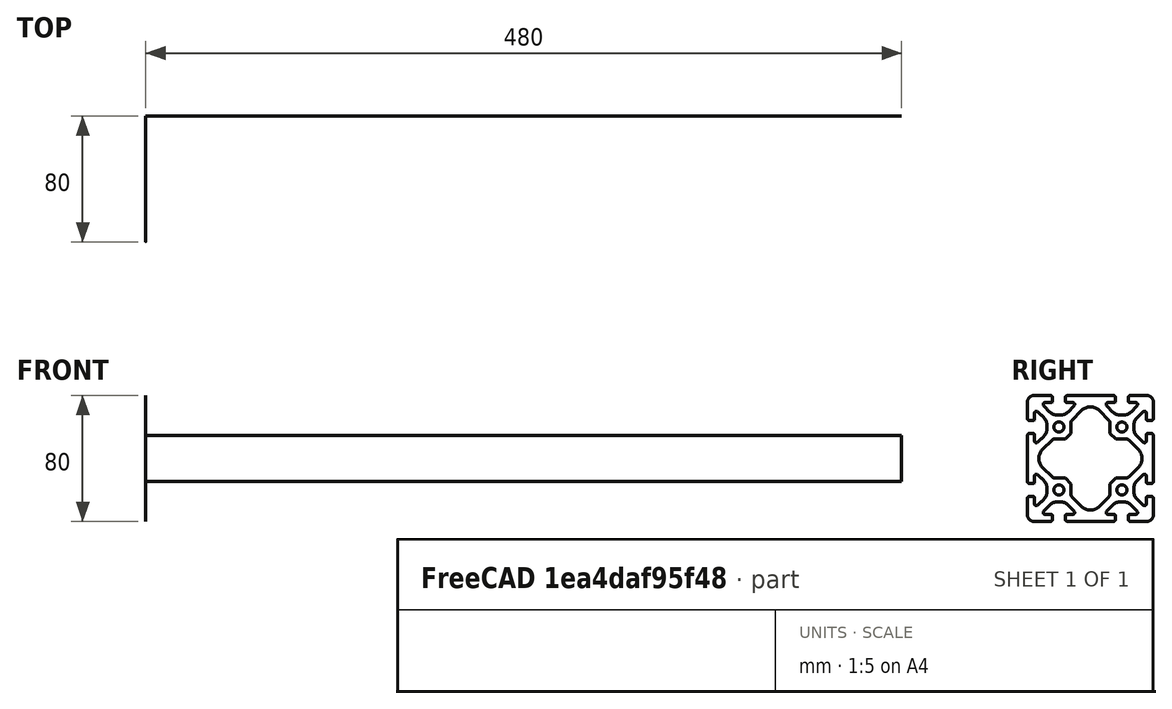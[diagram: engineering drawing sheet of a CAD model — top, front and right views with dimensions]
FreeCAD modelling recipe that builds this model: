
FCSTD DOCUMENT  (FreeCAD 0.21R38887 (Git))
Label: станок_сборка
License: All rights reserved
LicenseURL: http://en.wikipedia.org/wiki/All_rights_reserved
objects: App::FeaturePython×14, Part::FeaturePython×11, App::Link×2
note: 10 computed .brp shape members not serialized (recipe doc carries the construction recipe); baked Part::Feature solids carry a one-line shape summary decoded from their .brp
EXTERNAL_REF file=Станина/СтанинаСборка.FCStd obj=Assembly003
EXTERNAL_REF file=Стол/СборкаСтола.FCStd obj=Assembly

FEATURE [App::Link] Link  label="СборкаСтанины"
  AutoLinkLabel = false
  AutoPlacement = true
  LinkedObject = -> <external Станина/СтанинаСборка.FCStd>#Assembly003
  SyncGroupVisibility = false
  TreeRank = 0
  _LinkOwner = 31
  _LinkVersion = 1
FEATURE [App::Link] Link001  label="СборкаСтола"
  AutoLinkLabel = false
  AutoPlacement = true
  LinkPlacement = pos=(362.85,437.507,143.56) rot=(0.707107,0,0.707107;3.14159rad)
  LinkedObject = -> <external Стол/СборкаСтола.FCStd>#Assembly
  Placement = pos=(362.85,437.507,143.56) rot=(0.707107,0,0.707107;3.14159rad)
  SyncGroupVisibility = false
  TreeRank = 0
  _LinkOwner = 31
  _LinkVersion = 1
FEATURE [Part::FeaturePython] Parts  # WARN: FeaturePython — macro-defined, semantics opaque (R4)
  Group = -> [Link,Link001]
  GroupMode = 0
  InvalidShape = false
  TreeRank = 0
  ValidateShape = false
  _LinkVersion = 1
FEATURE [Part::FeaturePython] Assembly  # WARN: FeaturePython — macro-defined, semantics opaque (R4)
  AutoRelax = true
  BuildShape = 0
  Freeze = false
  Group = -> [Constraints,Elements,Parts]
  InvalidShape = false
  TreeRank = 0
  ValidateShape = false
  Verbose = false
  _LinkVersion = 1
  _SolverType = 1
  _Version = 1
FEATURE [App::FeaturePython] Constraints  # WARN: FeaturePython — macro-defined, semantics opaque (R4)
  Group = -> [Constraint001,Constraint,Constraint002]
  TreeRank = 0
  _LinkVersion = 1
  _Version = 1
FEATURE [App::FeaturePython] Elements  # WARN: FeaturePython — macro-defined, semantics opaque (R4)
  Group = -> [Element,Element001,_Element,_Element001,Element002,_Element002,_Element003,_Element004,_Element005]
  TreeRank = 0
  _LinkVersion = 1
FEATURE [Part::FeaturePython] Element  # link proxy (typed FeaturePython)
  Detach = false
  InvalidShape = false
  LinkTransform = true
  LinkedObject = -> Link [1.$Element152.]
  TreeRank = 0
  ValidateShape = false
  _LinkVersion = 1
  _Parent = -> Elements
FEATURE [Part::FeaturePython] Element001  # link proxy (typed FeaturePython)
  Detach = false
  InvalidShape = false
  LinkTransform = true
  LinkedObject = -> Link001 [1.$Element029.]
  TreeRank = 0
  ValidateShape = false
  _LinkVersion = 1
  _Parent = -> Elements
FEATURE [App::FeaturePython] Constraint  label="AxialAlignment"  # WARN: FeaturePython — macro-defined, semantics opaque (R4)
  Angle = 0
  AnglePitch = 0
  AngleRoll = 0
  Disabled = false
  Group = -> [ElementLink,ElementLink001,ElementLink005,ElementLink006,ElementLink009,ElementLink010]
  LockAngle = false
  Multiply = false
  TreeRank = 0
  _ConstraintType = 36
  _LinkVersion = 1
  _Parent = -> Constraints
FEATURE [App::FeaturePython] ElementLink  label="Element001"  # link proxy (typed FeaturePython)
  LinkTransform = true
  LinkedObject = -> Element001
  TreeRank = 0
  _LinkVersion = 1
  _Parent = -> Constraint
FEATURE [App::FeaturePython] ElementLink001  label="Element"  # link proxy (typed FeaturePython)
  LinkTransform = true
  LinkedObject = -> Element
  TreeRank = 0
  _LinkVersion = 1
  _Parent = -> Constraint
FEATURE [App::FeaturePython] Constraint001  label="Locked"  # WARN: FeaturePython — macro-defined, semantics opaque (R4)
  Disabled = false
  Group = -> [ElementLink002]
  TreeRank = 0
  _ConstraintType = 0
  _LinkVersion = 1
  _Parent = -> Constraints
FEATURE [App::FeaturePython] ElementLink002  label="_Element"  # link proxy (typed FeaturePython)
  LinkTransform = true
  LinkedObject = -> _Element
  TreeRank = 0
  _LinkVersion = 1
  _Parent = -> Constraint001
FEATURE [Part::FeaturePython] _Element  # link proxy (typed FeaturePython)
  Detach = false
  InvalidShape = false
  LinkTransform = true
  LinkedObject = -> Link [1.$Element154.]
  TreeRank = 0
  ValidateShape = false
  _LinkVersion = 1
  _Parent = -> Elements
FEATURE [App::FeaturePython] Constraint002  label="LineHorizontal"  # WARN: FeaturePython — macro-defined, semantics opaque (R4)
  Disabled = false
  Group = -> [ElementLink003,ElementLink004]
  TreeRank = 0
  _ConstraintType = 23
  _LinkVersion = 1
  _Parent = -> Constraints
FEATURE [App::FeaturePython] ElementLink003  label="_Element001"  # link proxy (typed FeaturePython)
  LinkTransform = true
  LinkedObject = -> _Element001
  TreeRank = 0
  _LinkVersion = 1
  _Parent = -> Constraint002
FEATURE [Part::FeaturePython] _Element001  # link proxy (typed FeaturePython)
  Detach = false
  InvalidShape = false
  LinkTransform = true
  LinkedObject = -> Link001 [1.$Element030.]
  TreeRank = 0
  ValidateShape = false
  _LinkVersion = 1
  _Parent = -> Elements
FEATURE [Part::FeaturePython] Element002  # link proxy (typed FeaturePython)
  Detach = false
  InvalidShape = false
  LinkTransform = true
  LinkedObject = -> Link [1.$_Element020.]
  TreeRank = 0
  ValidateShape = false
  _LinkVersion = 1
  _Parent = -> Elements
FEATURE [App::FeaturePython] ElementLink004  label="Element002"  # link proxy (typed FeaturePython)
  LinkTransform = true
  LinkedObject = -> Element002
  TreeRank = 0
  _LinkVersion = 1
  _Parent = -> Constraint002
FEATURE [App::FeaturePython] ElementLink005  label="_Element002"  # link proxy (typed FeaturePython)
  LinkTransform = true
  LinkedObject = -> _Element002
  TreeRank = 0
  _LinkVersion = 1
  _Parent = -> Constraint
FEATURE [Part::FeaturePython] _Element002  # link proxy (typed FeaturePython)
  Detach = false
  InvalidShape = false
  LinkTransform = true
  LinkedObject = -> Link001 [1.$Element031.]
  TreeRank = 0
  ValidateShape = false
  _LinkVersion = 1
  _Parent = -> Elements
FEATURE [App::FeaturePython] ElementLink006  label="_Element003"  # link proxy (typed FeaturePython)
  LinkTransform = true
  LinkedObject = -> _Element003
  TreeRank = 0
  _LinkVersion = 1
  _Parent = -> Constraint
FEATURE [Part::FeaturePython] _Element003  # link proxy (typed FeaturePython)
  Detach = false
  InvalidShape = false
  LinkTransform = true
  LinkedObject = -> Link [1.$Element156.]
  TreeRank = 0
  ValidateShape = false
  _LinkVersion = 1
  _Parent = -> Elements
FEATURE [App::FeaturePython] ElementLink009  label="_Element004"  # link proxy (typed FeaturePython)
  LinkTransform = true
  LinkedObject = -> _Element004
  TreeRank = 0
  _LinkVersion = 1
  _Parent = -> Constraint
FEATURE [Part::FeaturePython] _Element004  # link proxy (typed FeaturePython)
  Detach = false
  InvalidShape = false
  LinkTransform = true
  LinkedObject = -> Link001 [1.$Element032.]
  TreeRank = 0
  ValidateShape = false
  _LinkVersion = 1
  _Parent = -> Elements
FEATURE [App::FeaturePython] ElementLink010  label="_Element005"  # link proxy (typed FeaturePython)
  LinkTransform = true
  LinkedObject = -> _Element005
  TreeRank = 0
  _LinkVersion = 1
  _Parent = -> Constraint
FEATURE [Part::FeaturePython] _Element005  # link proxy (typed FeaturePython)
  Detach = false
  InvalidShape = false
  LinkTransform = true
  LinkedObject = -> Link [1.$Element158.]
  TreeRank = 0
  ValidateShape = false
  _LinkVersion = 1
  _Parent = -> Elements

RESOLVED EXTERNAL PARTS (link-assembly join: the EXTERNAL_REF files above that resolve inside this repo's crawl, each included once):
---- part Станина/СтанинаСборка.FCStd = doc fcstd_94fc6bfe06bf (92996 chars; too large to inline — full recipe in that document) ----
---- part Стол/СборкаСтола.FCStd = doc fcstd_60361f81c97c ----
FCSTD DOCUMENT  (FreeCAD 0.21R38887 (Git))
Label: СборкаСтола
License: All rights reserved
LicenseURL: http://en.wikipedia.org/wiki/All_rights_reserved
objects: App::FeaturePython×55, Part::FeaturePython×49, App::Link×4, App::LinkElement×4
note: 48 computed .brp shape members not serialized (recipe doc carries the construction recipe); baked Part::Feature solids carry a one-line shape summary decoded from their .brp
EXTERNAL_REF file=КронштейнГайки.FCStd obj=Body
EXTERNAL_REF file=Стол.FCStd obj=Body
EXTERNAL_REF file=HGH15CA.FCStd obj=Assembly
EXTERNAL_REF file=SFU1605.FCStd obj=Assembly

FEATURE [App::Link] Link  label="КронштейнГайкиX"
  AutoLinkLabel = false
  AutoPlacement = true
  LinkPlacement = pos=(-14.5,47,14.5) rot=(-0.707107,0,-0.707107;3.14159rad)
  LinkedObject = -> <external КронштейнГайки.FCStd>#Body
  Placement = pos=(-14.5,47,14.5) rot=(-0.707107,0,-0.707107;3.14159rad)
  SyncGroupVisibility = false
  TreeRank = 0
  _LinkOwner = 3680
  _LinkVersion = 1
FEATURE [App::Link] Link001  label="Body"
  AutoLinkLabel = false
  AutoPlacement = true
  LinkPlacement = pos=(3.2e-15,-0.5,14.5) rot=(-0.57735,-0.57735,-0.57735;2.0944rad)
  LinkedObject = -> <external Стол.FCStd>#Body
  Placement = pos=(3.2e-15,-0.5,14.5) rot=(-0.57735,-0.57735,-0.57735;2.0944rad)
  SyncGroupVisibility = false
  TreeRank = 0
  _LinkOwner = 3680
  _LinkVersion = 1
FEATURE [App::LinkElement] Link002_i0
  LinkPlacement = pos=(22.599,53.5,-77.5) rot=(0.57735,0.57735,-0.57735;2.0944rad)
  LinkedObject = -> <external HGH15CA.FCStd>#Assembly
  Placement = pos=(22.599,53.5,-77.5) rot=(0.57735,0.57735,-0.57735;2.0944rad)
  TreeRank = 86
  _LinkOwner = 3775
  _LinkVersion = 1
FEATURE [App::LinkElement] Link002_i1
  LinkPlacement = pos=(-84.001,53.5,-77.5) rot=(-0.57735,-0.57735,0.57735;4.18879rad)
  LinkedObject = -> <external HGH15CA.FCStd>#Assembly
  Placement = pos=(-84.001,53.5,-77.5) rot=(-0.57735,-0.57735,0.57735;4.18879rad)
  TreeRank = 87
  _LinkOwner = 3775
  _LinkVersion = 1
FEATURE [App::LinkElement] Link002_i2
  LinkPlacement = pos=(84.001,53.5,106.5) rot=(-0.57735,0.57735,-0.57735;4.18879rad)
  LinkedObject = -> <external HGH15CA.FCStd>#Assembly
  Placement = pos=(84.001,53.5,106.5) rot=(-0.57735,0.57735,-0.57735;4.18879rad)
  TreeRank = 88
  _LinkOwner = 3775
  _LinkVersion = 1
FEATURE [App::LinkElement] Link002_i3
  LinkPlacement = pos=(-22.599,53.5,106.5) rot=(0.57735,-0.57735,0.57735;2.0944rad)
  LinkedObject = -> <external HGH15CA.FCStd>#Assembly
  Placement = pos=(-22.599,53.5,106.5) rot=(0.57735,-0.57735,0.57735;2.0944rad)
  TreeRank = 89
  _LinkOwner = 3775
  _LinkVersion = 1
FEATURE [App::Link] Link002  label="HGH15CA"
  AutoLinkLabel = false
  AutoPlacement = true
  ElementCount = 4
  ElementList = -> [Link002_i0,Link002_i1,Link002_i2,Link002_i3]
  LinkedObject = -> <external HGH15CA.FCStd>#Assembly
  SyncGroupVisibility = false
  TreeRank = 85
  _LinkOwner = 3680
  _LinkVersion = 1
FEATURE [App::Link] Link003  label="SFU1606"
  AutoLinkLabel = false
  AutoPlacement = true
  LinkPlacement = pos=(-24.5,47,14.5) rot=(0,-1,0;1.5708rad)
  LinkedObject = -> <external SFU1605.FCStd>#Assembly
  Placement = pos=(-24.5,47,14.5) rot=(0,-1,0;1.5708rad)
  SyncGroupVisibility = false
  TreeRank = 138
  _LinkOwner = 3680
  _LinkVersion = 1
FEATURE [Part::FeaturePython] Parts  # WARN: FeaturePython — macro-defined, semantics opaque (R4)
  Group = -> [Link,Link001,Link002,Link003]
  GroupMode = 0
  InvalidShape = false
  TreeRank = 0
  ValidateShape = false
  _LinkVersion = 1
FEATURE [Part::FeaturePython] Assembly  # WARN: FeaturePython — macro-defined, semantics opaque (R4)
  AutoRelax = true
  BuildShape = 0
  Freeze = false
  Group = -> [Constraints,Elements,Parts]
  InvalidShape = false
  TreeRank = 0
  ValidateShape = false
  Verbose = false
  _LinkVersion = 1
  _SolverType = 1
  _Version = 1
FEATURE [App::FeaturePython] Constraints  # WARN: FeaturePython — macro-defined, semantics opaque (R4)
  Group = -> [Constraint001,Constraint,Constraint002,Constraint003,Constraint004,Constraint005,Constraint006,Constraint007,Constraint008,Constraint009,Constraint010,Constraint011,Constraint012,Constraint013,Constraint014,Constraint015,Constraint016,Constraint017]
  TreeRank = 0
  _LinkVersion = 1
  _Version = 1
FEATURE [App::FeaturePython] Elements  # WARN: FeaturePython — macro-defined, semantics opaque (R4)
  Group = -> [Element,Element001,_Element,_Element001,_Element002,Element002,Element003,Element004,Element005,Element006,Element007,Element008,Element009,Element010,Element011,Element012,Element013,Element014,Element015,Element016,Element018,Element019,Element020,Element021,Element022,Element023,Element024,_Element003,_Element004,_Element005,_Element006,_Element007,_Element008,_Element009,_Element010,+12 more]
  TreeRank = 0
  _LinkVersion = 1
FEATURE [Part::FeaturePython] Element  label="ПосадкаКронштейна"  # link proxy (typed FeaturePython)
  Detach = false
  InvalidShape = false
  LinkTransform = true
  LinkedObject = -> Link001 [Hole001.Face104]
  TreeRank = 2
  ValidateShape = false
  _LinkVersion = 1
  _Parent = -> Elements
FEATURE [Part::FeaturePython] Element001  label="КронштейнКСтолу"  # link proxy (typed FeaturePython)
  Detach = false
  InvalidShape = false
  LinkTransform = true
  LinkedObject = -> Link [Chamfer.Face2]
  Offset = pos=(0,0,0) rot=(1,0,0;3.14159rad)
  Placement = pos=(-1.65931e-09,47,2.63617e-09) rot=(0,0,1;3.14159rad)
  TreeRank = 3
  ValidateShape = false
  _LinkVersion = 1
  _Parent = -> Elements
FEATURE [App::FeaturePython] Constraint001  label="Locked"  # WARN: FeaturePython — macro-defined, semantics opaque (R4)
  Disabled = false
  Group = -> [ElementLink002]
  TreeRank = 7
  _ConstraintType = 0
  _LinkVersion = 1
  _Parent = -> Constraints
FEATURE [App::FeaturePython] ElementLink002  label="ФиксацияПоложенияСтола"  # link proxy (typed FeaturePython)
  LinkTransform = true
  LinkedObject = -> _Element
  TreeRank = 8
  _LinkVersion = 1
  _Parent = -> Constraint001
FEATURE [Part::FeaturePython] _Element  label="ФиксацияПоложенияСтола"  # link proxy (typed FeaturePython)
  Detach = false
  InvalidShape = false
  LinkTransform = true
  LinkedObject = -> Link001 [Hole001.Face51]
  TreeRank = 9
  ValidateShape = false
  _LinkVersion = 1
  _Parent = -> Elements
FEATURE [Part::FeaturePython] _Element001  # link proxy (typed FeaturePython)
  Detach = false
  InvalidShape = false
  LinkTransform = true
  LinkedObject = -> Link [Chamfer.Face14]
  TreeRank = 12
  ValidateShape = false
  _LinkVersion = 1
  _Parent = -> Elements
FEATURE [Part::FeaturePython] _Element002  # link proxy (typed FeaturePython)
  Detach = false
  InvalidShape = false
  LinkTransform = true
  LinkedObject = -> Link001 [Hole001.Face93]
  TreeRank = 14
  ValidateShape = false
  _LinkVersion = 1
  _Parent = -> Elements
FEATURE [App::FeaturePython] Constraint  label="PlaneAlignment"  # WARN: FeaturePython — macro-defined, semantics opaque (R4)
  Angle = 0
  AnglePitch = 0
  AngleRoll = 0
  Cascade = false
  Disabled = false
  Group = -> [ElementLink,ElementLink005]
  LockAngle = false
  TreeRank = 18
  _ConstraintType = 37
  _LinkVersion = 1
  _Parent = -> Constraints
FEATURE [App::FeaturePython] ElementLink  label="КронштейнКСтолу"  # link proxy (typed FeaturePython)
  LinkTransform = true
  LinkedObject = -> Element001
  TreeRank = 19
  _LinkVersion = 1
  _Parent = -> Constraint
FEATURE [App::FeaturePython] ElementLink005  label="ПосадкаКронштейна"  # link proxy (typed FeaturePython)
  LinkTransform = true
  LinkedObject = -> Element
  TreeRank = 20
  _LinkVersion = 1
  _Parent = -> Constraint
FEATURE [App::FeaturePython] Constraint002  label="PlaneAlignment001"  # WARN: FeaturePython — macro-defined, semantics opaque (R4)
  Angle = 0
  AnglePitch = 0
  AngleRoll = 0
  Cascade = false
  Disabled = false
  Group = -> [ElementLink006,ElementLink007]
  LockAngle = false
  TreeRank = 21
  _ConstraintType = 37
  _LinkVersion = 1
  _Parent = -> Constraints
FEATURE [App::FeaturePython] ElementLink006  label="_Element001"  # link proxy (typed FeaturePython)
  LinkTransform = true
  LinkedObject = -> _Element001
  TreeRank = 22
  _LinkVersion = 1
  _Parent = -> Constraint002
FEATURE [App::FeaturePython] ElementLink007  label="_Element002"  # link proxy (typed FeaturePython)
  LinkTransform = true
  LinkedObject = -> _Element002
  TreeRank = 23
  _LinkVersion = 1
  _Parent = -> Constraint002
FEATURE [Part::FeaturePython] Element002  label="ОтверстиеВКроншт"  # link proxy (typed FeaturePython)
  Detach = false
  InvalidShape = false
  LinkTransform = true
  LinkedObject = -> Link [Chamfer.Face22]
  TreeRank = 24
  ValidateShape = false
  _LinkVersion = 1
  _Parent = -> Elements
FEATURE [Part::FeaturePython] Element003  label="ОтверстиеСТолКроншт"  # link proxy (typed FeaturePython)
  Detach = false
  InvalidShape = false
  LinkTransform = true
  LinkedObject = -> Link001 [Hole001.Face103]
  TreeRank = 25
  ValidateShape = false
  _LinkVersion = 1
  _Parent = -> Elements
FEATURE [App::FeaturePython] Constraint003  label="AxialAlignment"  # WARN: FeaturePython — macro-defined, semantics opaque (R4)
  Angle = 0
  AnglePitch = 0
  AngleRoll = 0
  Disabled = false
  Group = -> [ElementLink008,ElementLink009]
  LockAngle = false
  Multiply = false
  TreeRank = 26
  _ConstraintType = 36
  _LinkVersion = 1
  _Parent = -> Constraints
FEATURE [App::FeaturePython] ElementLink008  label="ОтверстиеСТолКроншт"  # link proxy (typed FeaturePython)
  LinkTransform = true
  LinkedObject = -> Element003
  TreeRank = 27
  _LinkVersion = 1
  _Parent = -> Constraint003
FEATURE [App::FeaturePython] ElementLink009  label="ОтверстиеВКроншт"  # link proxy (typed FeaturePython)
  LinkTransform = true
  LinkedObject = -> Element002
  TreeRank = 28
  _LinkVersion = 1
  _Parent = -> Constraint003
FEATURE [Part::FeaturePython] Element004  label="ПлоскостьКареток1и2"  # link proxy (typed FeaturePython)
  Detach = false
  InvalidShape = false
  LinkTransform = true
  LinkedObject = -> Link001 [Hole001.Face47]
  TreeRank = 34
  ValidateShape = false
  _LinkVersion = 1
  _Parent = -> Elements
FEATURE [Part::FeaturePython] Element005  label="ПлоскостьКареток3и4"  # link proxy (typed FeaturePython)
  Detach = false
  InvalidShape = false
  LinkTransform = true
  LinkedObject = -> Link001 [Hole001.Face48]
  TreeRank = 35
  ValidateShape = false
  _LinkVersion = 1
  _Parent = -> Elements
FEATURE [Part::FeaturePython] Element006  label="БоковаяПлоскостьКареток1и2"  # link proxy (typed FeaturePython)
  Detach = false
  InvalidShape = false
  LinkTransform = true
  LinkedObject = -> Link001 [Hole001.Face74]
  TreeRank = 36
  ValidateShape = false
  _LinkVersion = 1
  _Parent = -> Elements
FEATURE [Part::FeaturePython] Element007  label="БоковаяПлоскостьКареток3и4"  # link proxy (typed FeaturePython)
  Detach = false
  InvalidShape = false
  LinkTransform = true
  LinkedObject = -> Link001 [Hole001.Face83]
  TreeRank = 37
  ValidateShape = false
  _LinkVersion = 1
  _Parent = -> Elements
FEATURE [Part::FeaturePython] Element008  label="СтолКареткаОтв1"  # link proxy (typed FeaturePython)
  Detach = false
  InvalidShape = false
  LinkTransform = true
  LinkedObject = -> Link001 [Hole001.Face80]
  TreeRank = 38
  ValidateShape = false
  _LinkVersion = 1
  _Parent = -> Elements
FEATURE [Part::FeaturePython] Element009  label="СтолКареткаОтв2"  # link proxy (typed FeaturePython)
  Detach = false
  InvalidShape = false
  LinkTransform = true
  LinkedObject = -> Link001 [Hole001.Face82]
  TreeRank = 39
  ValidateShape = false
  _LinkVersion = 1
  _Parent = -> Elements
FEATURE [Part::FeaturePython] Element010  label="СтолКареткаОтв3"  # link proxy (typed FeaturePython)
  Detach = false
  InvalidShape = false
  LinkTransform = true
  LinkedObject = -> Link001 [Hole001.Face81]
  TreeRank = 40
  ValidateShape = false
  _LinkVersion = 1
  _Parent = -> Elements
FEATURE [Part::FeaturePython] Element011  label="СтолКареткаОтв4"  # link proxy (typed FeaturePython)
  Detach = false
  InvalidShape = false
  LinkTransform = true
  LinkedObject = -> Link001 [Hole001.Face79]
  TreeRank = 41
  ValidateShape = false
  _LinkVersion = 1
  _Parent = -> Elements
FEATURE [Part::FeaturePython] Element012  label="СтолКаретка2Отв1"  # link proxy (typed FeaturePython)
  Detach = false
  InvalidShape = false
  LinkTransform = true
  LinkedObject = -> Link001 [Hole001.Face76]
  TreeRank = 42
  ValidateShape = false
  _LinkVersion = 1
  _Parent = -> Elements
FEATURE [Part::FeaturePython] Element013  label="СтолКаретка2Отв2"  # link proxy (typed FeaturePython)
  Detach = false
  InvalidShape = false
  LinkTransform = true
  LinkedObject = -> Link001 [Hole001.Face78]
  TreeRank = 43
  ValidateShape = false
  _LinkVersion = 1
  _Parent = -> Elements
FEATURE [Part::FeaturePython] Element014  label="СтолКаретка2Отв3"  # link proxy (typed FeaturePython)
  Detach = false
  InvalidShape = false
  LinkTransform = true
  LinkedObject = -> Link001 [Hole001.Face77]
  TreeRank = 44
  ValidateShape = false
  _LinkVersion = 1
  _Parent = -> Elements
FEATURE [Part::FeaturePython] Element015  label="СтолКаретка2Отв4"  # link proxy (typed FeaturePython)
  Detach = false
  InvalidShape = false
  LinkTransform = true
  LinkedObject = -> Link001 [Hole001.Face75]
  TreeRank = 45
  ValidateShape = false
  _LinkVersion = 1
  _Parent = -> Elements
FEATURE [Part::FeaturePython] Element016  label="СтолКаретка3Отв1"  # link proxy (typed FeaturePython)
  Detach = false
  InvalidShape = false
  LinkTransform = true
  LinkedObject = -> Link001 [Hole001.Face91]
  TreeRank = 76
  ValidateShape = false
  _LinkVersion = 1
  _Parent = -> Elements
FEATURE [Part::FeaturePython] Element018  label="СтолКаретка3Отв4"  # link proxy (typed FeaturePython)
  Detach = false
  InvalidShape = false
  LinkTransform = true
  LinkedObject = -> Link001 [Hole001.Face90]
  TreeRank = 78
  ValidateShape = false
  _LinkVersion = 1
  _Parent = -> Elements
FEATURE [Part::FeaturePython] Element019  label="СтолКаретка3Отв3"  # link proxy (typed FeaturePython)
  Detach = false
  InvalidShape = false
  LinkTransform = true
  LinkedObject = -> Link001 [Hole001.Face88]
  TreeRank = 79
  ValidateShape = false
  _LinkVersion = 1
  _Parent = -> Elements
FEATURE [Part::FeaturePython] Element020  label="СтолКаретка3Отв2"  # link proxy (typed FeaturePython)
  Detach = false
  InvalidShape = false
  LinkTransform = true
  LinkedObject = -> Link001 [Hole001.Face89]
  TreeRank = 80
  ValidateShape = false
  _LinkVersion = 1
  _Parent = -> Elements
FEATURE [Part::FeaturePython] Element021  label="СтолКаретка4Отв1"  # link proxy (typed FeaturePython)
  Detach = false
  InvalidShape = false
  LinkTransform = true
  LinkedObject = -> Link001 [Hole001.Face87]
  TreeRank = 81
  ValidateShape = false
  _LinkVersion = 1
  _Parent = -> Elements
FEATURE [Part::FeaturePython] Element022  label="СтолКаретка4Отв2"  # link proxy (typed FeaturePython)
  Detach = false
  InvalidShape = false
  LinkTransform = true
  LinkedObject = -> Link001 [Hole001.Face85]
  TreeRank = 82
  ValidateShape = false
  _LinkVersion = 1
  _Parent = -> Elements
FEATURE [Part::FeaturePython] Element023  label="СтолКаретка4Отв4"  # link proxy (typed FeaturePython)
  Detach = false
  InvalidShape = false
  LinkTransform = true
  LinkedObject = -> Link001 [Hole001.Face86]
  TreeRank = 83
  ValidateShape = false
  _LinkVersion = 1
  _Parent = -> Elements
FEATURE [Part::FeaturePython] Element024  label="СтолКаретка4Отв3"  # link proxy (typed FeaturePython)
  Detach = false
  InvalidShape = false
  LinkTransform = true
  LinkedObject = -> Link001 [Hole001.Face84]
  TreeRank = 84
  ValidateShape = false
  _LinkVersion = 1
  _Parent = -> Elements
FEATURE [App::FeaturePython] Constraint004  label="PlaneAlignment002"  # WARN: FeaturePython — macro-defined, semantics opaque (R4)
  Angle = 0
  AnglePitch = 0
  AngleRoll = 0
  Cascade = false
  Disabled = false
  Group = -> [ElementLink010,ElementLink011]
  LockAngle = false
  TreeRank = 90
  _ConstraintType = 37
  _LinkVersion = 1
  _Parent = -> Constraints
FEATURE [App::FeaturePython] ElementLink010  label="БоковаяПласкостьПрилегания@HGH15CA@#0"  # link proxy (typed FeaturePython)
  LinkTransform = true
  LinkedObject = -> _Element003
  TreeRank = 91
  _LinkVersion = 1
  _Parent = -> Constraint004
FEATURE [Part::FeaturePython] _Element003  label="БоковаяПласкостьПрилегания@HGH15CA@#0"  # link proxy (typed FeaturePython)
  Detach = false
  InvalidShape = false
  LinkTransform = true
  LinkedObject = -> Link002 [Link002_i0.1.$БоковаяПласкостьПрилегания.]
  TreeRank = 92
  ValidateShape = false
  _LinkVersion = 1
  _Parent = -> Elements
FEATURE [App::FeaturePython] ElementLink011  label="БоковаяПлоскостьКареток1и2"  # link proxy (typed FeaturePython)
  LinkTransform = true
  LinkedObject = -> Element006
  TreeRank = 93
  _LinkVersion = 1
  _Parent = -> Constraint004
FEATURE [App::FeaturePython] Constraint005  label="PlaneAlignment003"  # WARN: FeaturePython — macro-defined, semantics opaque (R4)
  Angle = 0
  AnglePitch = 0
  AngleRoll = 0
  Cascade = false
  Disabled = false
  Group = -> [ElementLink012,ElementLink013]
  LockAngle = false
  TreeRank = 94
  _ConstraintType = 37
  _LinkVersion = 1
  _Parent = -> Constraints
FEATURE [App::FeaturePython] ElementLink012  label="ПлоскостьПрилегания@HGH15CA@#0"  # link proxy (typed FeaturePython)
  LinkTransform = true
  LinkedObject = -> _Element004
  TreeRank = 95
  _LinkVersion = 1
  _Parent = -> Constraint005
FEATURE [Part::FeaturePython] _Element004  label="ПлоскостьПрилегания@HGH15CA@#0"  # link proxy (typed FeaturePython)
  Detach = false
  InvalidShape = false
  LinkTransform = true
  LinkedObject = -> Link002 [Link002_i0.1.$ПлоскостьПрилегания.]
  TreeRank = 96
  ValidateShape = false
  _LinkVersion = 1
  _Parent = -> Elements
FEATURE [App::FeaturePython] ElementLink013  label="ПлоскостьКареток1и2"  # link proxy (typed FeaturePython)
  LinkTransform = true
  LinkedObject = -> Element004
  TreeRank = 97
  _LinkVersion = 1
  _Parent = -> Constraint005
FEATURE [App::FeaturePython] Constraint006  label="AxialAlignment001"  # WARN: FeaturePython — macro-defined, semantics opaque (R4)
  Angle = 0
  AnglePitch = 0
  AngleRoll = 0
  Disabled = false
  Group = -> [ElementLink014,ElementLink015]
  LockAngle = false
  Multiply = false
  TreeRank = 98
  _ConstraintType = 36
  _LinkVersion = 1
  _Parent = -> Constraints
FEATURE [App::FeaturePython] ElementLink014  label="Отв1@HGH15CA@#0"  # link proxy (typed FeaturePython)
  LinkTransform = true
  LinkedObject = -> _Element005
  TreeRank = 99
  _LinkVersion = 1
  _Parent = -> Constraint006
FEATURE [Part::FeaturePython] _Element005  label="Отв1@HGH15CA@#0"  # link proxy (typed FeaturePython)
  Detach = false
  InvalidShape = false
  LinkTransform = true
  LinkedObject = -> Link002 [Link002_i0.1.$Отв1.]
  TreeRank = 100
  ValidateShape = false
  _LinkVersion = 1
  _Parent = -> Elements
FEATURE [App::FeaturePython] ElementLink015  label="СтолКареткаОтв2"  # link proxy (typed FeaturePython)
  LinkTransform = true
  LinkedObject = -> Element009
  TreeRank = 101
  _LinkVersion = 1
  _Parent = -> Constraint006
FEATURE [App::FeaturePython] Constraint007  label="PlaneAlignment004"  # WARN: FeaturePython — macro-defined, semantics opaque (R4)
  Angle = 0
  AnglePitch = 0
  AngleRoll = 0
  Cascade = false
  Disabled = false
  Group = -> [ElementLink016,ElementLink017]
  LockAngle = false
  TreeRank = 102
  _ConstraintType = 37
  _LinkVersion = 1
  _Parent = -> Constraints
FEATURE [App::FeaturePython] ElementLink016  label="БоковаяПласкостьПрилегания@HGH15CA@#1"  # link proxy (typed FeaturePython)
  LinkTransform = true
  LinkedObject = -> _Element006
  TreeRank = 103
  _LinkVersion = 1
  _Parent = -> Constraint007
FEATURE [Part::FeaturePython] _Element006  label="БоковаяПласкостьПрилегания@HGH15CA@#1"  # link proxy (typed FeaturePython)
  Detach = false
  InvalidShape = false
  LinkTransform = true
  LinkedObject = -> Link002 [Link002_i1.1.$БоковаяПласкостьПрилегания.]
  TreeRank = 104
  ValidateShape = false
  _LinkVersion = 1
  _Parent = -> Elements
FEATURE [App::FeaturePython] ElementLink017  label="БоковаяПлоскостьКареток1и2"  # link proxy (typed FeaturePython)
  LinkTransform = true
  LinkedObject = -> Element006
  TreeRank = 105
  _LinkVersion = 1
  _Parent = -> Constraint007
FEATURE [App::FeaturePython] Constraint008  label="PlaneAlignment005"  # WARN: FeaturePython — macro-defined, semantics opaque (R4)
  Angle = 0
  AnglePitch = 0
  AngleRoll = 0
  Cascade = false
  Disabled = false
  Group = -> [ElementLink018,ElementLink019]
  LockAngle = false
  TreeRank = 106
  _ConstraintType = 37
  _LinkVersion = 1
  _Parent = -> Constraints
FEATURE [App::FeaturePython] ElementLink018  label="ПлоскостьПрилегания@HGH15CA@#1"  # link proxy (typed FeaturePython)
  LinkTransform = true
  LinkedObject = -> _Element007
  TreeRank = 107
  _LinkVersion = 1
  _Parent = -> Constraint008
FEATURE [Part::FeaturePython] _Element007  label="ПлоскостьПрилегания@HGH15CA@#1"  # link proxy (typed FeaturePython)
  Detach = false
  InvalidShape = false
  LinkTransform = true
  LinkedObject = -> Link002 [Link002_i1.1.$ПлоскостьПрилегания.]
  TreeRank = 108
  ValidateShape = false
  _LinkVersion = 1
  _Parent = -> Elements
FEATURE [App::FeaturePython] ElementLink019  label="ПлоскостьКареток1и2"  # link proxy (typed FeaturePython)
  LinkTransform = true
  LinkedObject = -> Element004
  TreeRank = 109
  _LinkVersion = 1
  _Parent = -> Constraint008
FEATURE [App::FeaturePython] Constraint009  label="AxialAlignment002"  # WARN: FeaturePython — macro-defined, semantics opaque (R4)
  Angle = 0
  AnglePitch = 0
  AngleRoll = 0
  Disabled = false
  Group = -> [ElementLink020,ElementLink021]
  LockAngle = false
  Multiply = false
  TreeRank = 110
  _ConstraintType = 36
  _LinkVersion = 1
  _Parent = -> Constraints
FEATURE [App::FeaturePython] ElementLink020  label="Отв1@HGH15CA@#1"  # link proxy (typed FeaturePython)
  LinkTransform = true
  LinkedObject = -> _Element008
  TreeRank = 111
  _LinkVersion = 1
  _Parent = -> Constraint009
FEATURE [Part::FeaturePython] _Element008  label="Отв1@HGH15CA@#1"  # link proxy (typed FeaturePython)
  Detach = false
  InvalidShape = false
  LinkTransform = true
  LinkedObject = -> Link002 [Link002_i1.1.$Отв1.]
  TreeRank = 112
  ValidateShape = false
  _LinkVersion = 1
  _Parent = -> Elements
FEATURE [App::FeaturePython] ElementLink021  label="СтолКаретка2Отв2"  # link proxy (typed FeaturePython)
  LinkTransform = true
  LinkedObject = -> Element013
  TreeRank = 113
  _LinkVersion = 1
  _Parent = -> Constraint009
FEATURE [App::FeaturePython] Constraint010  label="PlaneAlignment006"  # WARN: FeaturePython — macro-defined, semantics opaque (R4)
  Angle = 0
  AnglePitch = 0
  AngleRoll = 0
  Cascade = false
  Disabled = false
  Group = -> [ElementLink022,ElementLink023]
  LockAngle = false
  TreeRank = 114
  _ConstraintType = 37
  _LinkVersion = 1
  _Parent = -> Constraints
FEATURE [App::FeaturePython] ElementLink022  label="БоковаяПласкостьПрилегания@HGH15CA@#2"  # link proxy (typed FeaturePython)
  LinkTransform = true
  LinkedObject = -> _Element009
  TreeRank = 115
  _LinkVersion = 1
  _Parent = -> Constraint010
FEATURE [Part::FeaturePython] _Element009  label="БоковаяПласкостьПрилегания@HGH15CA@#2"  # link proxy (typed FeaturePython)
  Detach = false
  InvalidShape = false
  LinkTransform = true
  LinkedObject = -> Link002 [Link002_i2.1.$БоковаяПласкостьПрилегания.]
  TreeRank = 116
  ValidateShape = false
  _LinkVersion = 1
  _Parent = -> Elements
FEATURE [App::FeaturePython] ElementLink023  label="БоковаяПлоскостьКареток3и4"  # link proxy (typed FeaturePython)
  LinkTransform = true
  LinkedObject = -> Element007
  TreeRank = 117
  _LinkVersion = 1
  _Parent = -> Constraint010
FEATURE [App::FeaturePython] Constraint011  label="PlaneAlignment007"  # WARN: FeaturePython — macro-defined, semantics opaque (R4)
  Angle = 0
  AnglePitch = 0
  AngleRoll = 0
  Cascade = false
  Disabled = false
  Group = -> [ElementLink024,ElementLink025]
  LockAngle = false
  TreeRank = 118
  _ConstraintType = 37
  _LinkVersion = 1
  _Parent = -> Constraints
FEATURE [App::FeaturePython] ElementLink024  label="ПлоскостьПрилегания@HGH15CA@#2"  # link proxy (typed FeaturePython)
  LinkTransform = true
  LinkedObject = -> _Element010
  TreeRank = 119
  _LinkVersion = 1
  _Parent = -> Constraint011
FEATURE [Part::FeaturePython] _Element010  label="ПлоскостьПрилегания@HGH15CA@#2"  # link proxy (typed FeaturePython)
  Detach = false
  InvalidShape = false
  LinkTransform = true
  LinkedObject = -> Link002 [Link002_i2.1.$ПлоскостьПрилегания.]
  TreeRank = 120
  ValidateShape = false
  _LinkVersion = 1
  _Parent = -> Elements
FEATURE [App::FeaturePython] ElementLink025  label="ПлоскостьКареток3и4"  # link proxy (typed FeaturePython)
  LinkTransform = true
  LinkedObject = -> Element005
  TreeRank = 121
  _LinkVersion = 1
  _Parent = -> Constraint011
FEATURE [App::FeaturePython] Constraint012  label="AxialAlignment003"  # WARN: FeaturePython — macro-defined, semantics opaque (R4)
  Angle = 0
  AnglePitch = 0
  AngleRoll = 0
  Disabled = false
  Group = -> [ElementLink026,ElementLink027]
  LockAngle = false
  Multiply = false
  TreeRank = 122
  _ConstraintType = 36
  _LinkVersion = 1
  _Parent = -> Constraints
FEATURE [App::FeaturePython] ElementLink026  label="Отв1@HGH15CA@#2"  # link proxy (typed FeaturePython)
  LinkTransform = true
  LinkedObject = -> _Element011
  TreeRank = 123
  _LinkVersion = 1
  _Parent = -> Constraint012
FEATURE [Part::FeaturePython] _Element011  label="Отв1@HGH15CA@#2"  # link proxy (typed FeaturePython)
  Detach = false
  InvalidShape = false
  LinkTransform = true
  LinkedObject = -> Link002 [Link002_i2.1.$Отв1.]
  TreeRank = 124
  ValidateShape = false
  _LinkVersion = 1
  _Parent = -> Elements
FEATURE [App::FeaturePython] ElementLink027  label="СтолКаретка3Отв3"  # link proxy (typed FeaturePython)
  LinkTransform = true
  LinkedObject = -> Element019
  TreeRank = 125
  _LinkVersion = 1
  _Parent = -> Constraint012
FEATURE [App::FeaturePython] Constraint013  label="PlaneAlignment008"  # WARN: FeaturePython — macro-defined, semantics opaque (R4)
  Angle = 0
  AnglePitch = 0
  AngleRoll = 0
  Cascade = false
  Disabled = false
  Group = -> [ElementLink028,ElementLink029]
  LockAngle = false
  TreeRank = 126
  _ConstraintType = 37
  _LinkVersion = 1
  _Parent = -> Constraints
FEATURE [App::FeaturePython] ElementLink028  label="БоковаяПласкостьПрилегания@HGH15CA@#3"  # link proxy (typed FeaturePython)
  LinkTransform = true
  LinkedObject = -> _Element012
  TreeRank = 127
  _LinkVersion = 1
  _Parent = -> Constraint013
FEATURE [Part::FeaturePython] _Element012  label="БоковаяПласкостьПрилегания@HGH15CA@#3"  # link proxy (typed FeaturePython)
  Detach = false
  InvalidShape = false
  LinkTransform = true
  LinkedObject = -> Link002 [Link002_i3.1.$БоковаяПласкостьПрилегания.]
  TreeRank = 128
  ValidateShape = false
  _LinkVersion = 1
  _Parent = -> Elements
FEATURE [App::FeaturePython] ElementLink029  label="БоковаяПлоскостьКареток3и4"  # link proxy (typed FeaturePython)
  LinkTransform = true
  LinkedObject = -> Element007
  TreeRank = 129
  _LinkVersion = 1
  _Parent = -> Constraint013
FEATURE [App::FeaturePython] Constraint014  label="PlaneAlignment009"  # WARN: FeaturePython — macro-defined, semantics opaque (R4)
  Angle = 0
  AnglePitch = 0
  AngleRoll = 0
  Cascade = false
  Disabled = false
  Group = -> [ElementLink030,ElementLink031]
  LockAngle = false
  TreeRank = 130
  _ConstraintType = 37
  _LinkVersion = 1
  _Parent = -> Constraints
FEATURE [App::FeaturePython] ElementLink030  label="ПлоскостьПрилегания@HGH15CA@#3"  # link proxy (typed FeaturePython)
  LinkTransform = true
  LinkedObject = -> _Element013
  TreeRank = 131
  _LinkVersion = 1
  _Parent = -> Constraint014
FEATURE [Part::FeaturePython] _Element013  label="ПлоскостьПрилегания@HGH15CA@#3"  # link proxy (typed FeaturePython)
  Detach = false
  InvalidShape = false
  LinkTransform = true
  LinkedObject = -> Link002 [Link002_i3.1.$ПлоскостьПрилегания.]
  TreeRank = 132
  ValidateShape = false
  _LinkVersion = 1
  _Parent = -> Elements
FEATURE [App::FeaturePython] ElementLink031  label="ПлоскостьКареток3и4"  # link proxy (typed FeaturePython)
  LinkTransform = true
  LinkedObject = -> Element005
  TreeRank = 133
  _LinkVersion = 1
  _Parent = -> Constraint014
FEATURE [App::FeaturePython] Constraint015  label="AxialAlignment004"  # WARN: FeaturePython — macro-defined, semantics opaque (R4)
  Angle = 0
  AnglePitch = 0
  AngleRoll = 0
  Disabled = false
  Group = -> [ElementLink032,ElementLink033]
  LockAngle = false
  Multiply = false
  TreeRank = 134
  _ConstraintType = 36
  _LinkVersion = 1
  _Parent = -> Constraints
FEATURE [App::FeaturePython] ElementLink032  label="Отв1@HGH15CA@#3"  # link proxy (typed FeaturePython)
  LinkTransform = true
  LinkedObject = -> _Element014
  TreeRank = 135
  _LinkVersion = 1
  _Parent = -> Constraint015
FEATURE [Part::FeaturePython] _Element014  label="Отв1@HGH15CA@#3"  # link proxy (typed FeaturePython)
  Detach = false
  InvalidShape = false
  LinkTransform = true
  LinkedObject = -> Link002 [Link002_i3.1.$Отв1.]
  TreeRank = 136
  ValidateShape = false
  _LinkVersion = 1
  _Parent = -> Elements
FEATURE [App::FeaturePython] ElementLink033  label="СтолКаретка4Отв3"  # link proxy (typed FeaturePython)
  LinkTransform = true
  LinkedObject = -> Element024
  TreeRank = 137
  _LinkVersion = 1
  _Parent = -> Constraint015
FEATURE [Part::FeaturePython] Element025  label="ГайкаШВППосадка"  # link proxy (typed FeaturePython)
  Detach = false
  InvalidShape = false
  LinkTransform = true
  LinkedObject = -> Link003 [1.$Element.]
  TreeRank = 139
  ValidateShape = false
  _LinkVersion = 1
  _Parent = -> Elements
FEATURE [Part::FeaturePython] Element026  # link proxy (typed FeaturePython)
  Detach = false
  InvalidShape = false
  LinkTransform = true
  LinkedObject = -> Link003 [1.$Element001.]
  TreeRank = 140
  ValidateShape = false
  _LinkVersion = 1
  _Parent = -> Elements
FEATURE [Part::FeaturePython] Element027  # link proxy (typed FeaturePython)
  Detach = false
  InvalidShape = false
  LinkTransform = true
  LinkedObject = -> Link [Chamfer.Face55]
  TreeRank = 141
  ValidateShape = false
  _LinkVersion = 1
  _Parent = -> Elements
FEATURE [App::FeaturePython] Constraint016  label="AxialAlignment005"  # WARN: FeaturePython — macro-defined, semantics opaque (R4)
  Angle = 0
  AnglePitch = 0
  AngleRoll = 0
  Disabled = false
  Group = -> [ElementLink034,ElementLink035]
  LockAngle = false
  Multiply = false
  TreeRank = 142
  _ConstraintType = 36
  _LinkVersion = 1
  _Parent = -> Constraints
FEATURE [App::FeaturePython] ElementLink034  label="Element027"  # link proxy (typed FeaturePython)
  LinkTransform = true
  LinkedObject = -> Element027
  TreeRank = 143
  _LinkVersion = 1
  _Parent = -> Constraint016
FEATURE [App::FeaturePython] ElementLink035  label="Element026"  # link proxy (typed FeaturePython)
  LinkTransform = true
  LinkedObject = -> Element026
  TreeRank = 144
  _LinkVersion = 1
  _Parent = -> Constraint016
FEATURE [App::FeaturePython] Constraint017  label="PlaneAlignment010"  # WARN: FeaturePython — macro-defined, semantics opaque (R4)
  Angle = 0
  AnglePitch = 0
  AngleRoll = 0
  Cascade = false
  Disabled = false
  Group = -> [ElementLink036,ElementLink037]
  LockAngle = false
  TreeRank = 145
  _ConstraintType = 37
  _LinkVersion = 1
  _Parent = -> Constraints
FEATURE [App::FeaturePython] ElementLink036  label="ГайкаШВППосадка"  # link proxy (typed FeaturePython)
  LinkTransform = true
  LinkedObject = -> Element025
  TreeRank = 146
  _LinkVersion = 1
  _Parent = -> Constraint017
FEATURE [App::FeaturePython] ElementLink037  label="_Element001"  # link proxy (typed FeaturePython)
  LinkTransform = true
  LinkedObject = -> _Element001
  TreeRank = 147
  _LinkVersion = 1
  _Parent = -> Constraint017
FEATURE [Part::FeaturePython] Element028  # link proxy (typed FeaturePython)
  Detach = false
  InvalidShape = false
  LinkTransform = true
  LinkedObject = -> Link003 [1.$Element002.]
  TreeRank = 148
  ValidateShape = false
  _LinkVersion = 1
  _Parent = -> Elements
FEATURE [Part::FeaturePython] Element029  # link proxy (typed FeaturePython)
  Detach = false
  InvalidShape = false
  LinkTransform = true
  LinkedObject = -> Link003 [1.$Element003.]
  TreeRank = 149
  ValidateShape = false
  _LinkVersion = 1
  _Parent = -> Elements
FEATURE [Part::FeaturePython] Element030  # link proxy (typed FeaturePython)
  Detach = false
  InvalidShape = false
  LinkTransform = true
  LinkedObject = -> Link001 [Hole001.Edge13]
  TreeRank = 150
  ValidateShape = false
  _LinkVersion = 1
  _Parent = -> Elements
FEATURE [Part::FeaturePython] Element031  # link proxy (typed FeaturePython)
  Detach = false
  InvalidShape = false
  LinkTransform = true
  LinkedObject = -> Link001 [Hole001.Edge5]
  TreeRank = 151
  ValidateShape = false
  _LinkVersion = 1
  _Parent = -> Elements
FEATURE [Part::FeaturePython] Element032  # link proxy (typed FeaturePython)
  Detach = false
  InvalidShape = false
  LinkTransform = true
  LinkedObject = -> Link001 [Hole001.Edge42]
  TreeRank = 152
  ValidateShape = false
  _LinkVersion = 1
  _Parent = -> Elements
